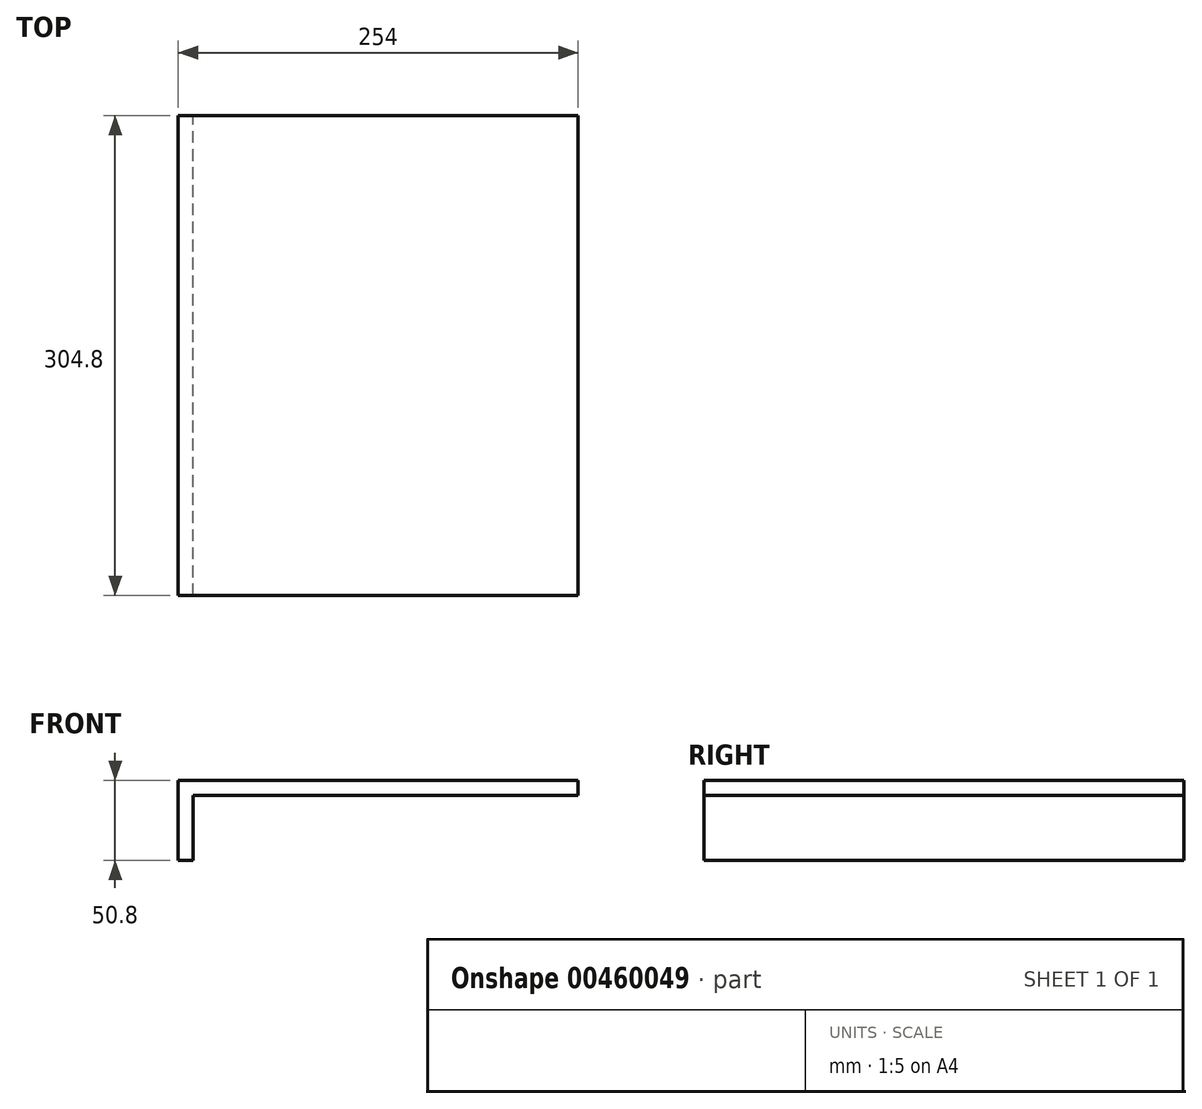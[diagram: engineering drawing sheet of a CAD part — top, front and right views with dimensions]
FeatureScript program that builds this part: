
annotation { "Feature Type Name" : "Feature", "Feature Type Description" : "" }
export const myFeature = defineFeature(function(context is Context, id is Id, definition is map)
    precondition{}
    {
        {
            var Q0;
            Q0=qCreatedBy(makeId("Front.planeOp"),FACE);
            var sketch = newSketch(context, id + "F0", { "sketchPlane" : qUnion([Q0])});
            skLineSegment(sketch, "E0", {"start": v(227.79, 30.58) * mm, "end": v(-26.21, 30.58) * mm});
            skLineSegment(sketch, "E1", {"start": v(-26.21, 30.58) * mm, "end": v(-26.21, -20.22) * mm});
            skLineSegment(sketch, "E2", {"start": v(-26.21, -20.22) * mm, "end": v(-16.69, -20.22) * mm});
            skLineSegment(sketch, "E3", {"start": v(-16.69, -20.22) * mm, "end": v(-16.69, 21.05) * mm});
            skLineSegment(sketch, "E4", {"start": v(-16.69, 21.05) * mm, "end": v(227.79, 21.05) * mm});
            skLineSegment(sketch, "E5", {"start": v(227.79, 21.05) * mm, "end": v(227.79, 30.58) * mm});
            skSolve(sketch);
        }
        {
            var Q0;
            Q0=makeQuery(id+"F0.imprint","IMPRINT",FACE,{"disambiguationData":[TD([[makeQuery(id+"F0.imprint","IMPRINT",EDGE,{"derivedFrom":sQuery(id+"F0.wireOp",EDGE,"E0")}),1.0]])]});
            extrude(context, id + "F1", {"entities" : qUnion([Q0]), "depth" : 304.8 * mm});
        }
    });
